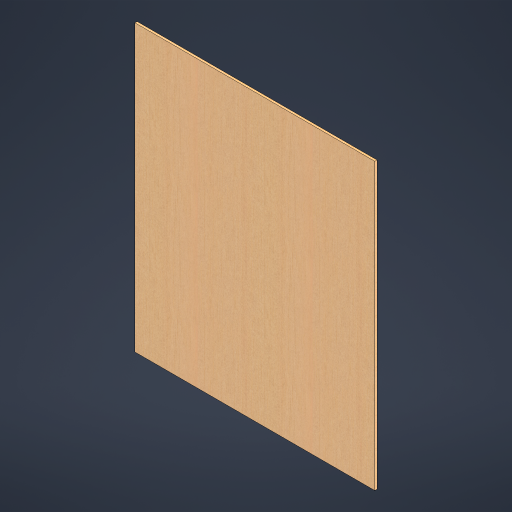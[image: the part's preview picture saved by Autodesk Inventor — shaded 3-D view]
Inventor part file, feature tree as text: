
AUTODESK INVENTOR PART (.ipt)
format: ipt  version: 2024 (Build 280153000, 153)  size: 314,368 bytes
history: native  units: mm
features: other x2, extrude x1, sketch x1
ambient origin geometry x8: Origin, YZ Plane, XZ Plane, XY Plane, X Axis, Y Axis, Z Axis, Center Point
bodies: Body1 (feature_tree)
feature tree (4):
  other  "솔리드1"
  extrude  "돌출1"  Depth=530.0mm
  sketch  "스케치1"
  other  "Finish1"
